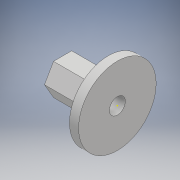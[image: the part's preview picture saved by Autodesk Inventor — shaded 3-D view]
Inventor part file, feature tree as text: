
AUTODESK INVENTOR PART (.ipt)
format: ipt  version: 2018 (Build 220112000, 112)  size: 129,536 bytes
history: native  units: mm
features: sketch x8, extrude x6
ambient origin geometry x8: Origin, YZ Plane, XZ Plane, XY Plane, X Axis, Y Axis, Z Axis, Center Point
bodies: Solid1 (feature_tree)
feature tree (14):
  extrude  "Extrusion1"  Depth=4.0mm TaperAngle=0.0deg
  extrude  "Extrusion2"  Depth=12.0mm
  sketch  "Sketch3"  dims[d6=2.0mm d7=0.0mm d8=3.0mm]
  extrude  "Extrusion3"  Depth=2.0mm
  extrude  "Extrusion4"  Depth=6.0mm
  sketch  "Sketch6"  dims[d16=3.5mm d17=12.25mm d18=0.0mm]
  extrude  "Extrusion5"  Depth=6.0mm TaperAngle=0.0deg
  extrude  "Extrusion6"  Depth=12.25mm TaperAngle=0.0deg
  sketch  "Sketch1"  dims[d0=4.0mm d1=4.0mm d2=0.0mm]
  sketch  "Sketch2"  dims[d3=2.0mm d4=0.0mm d5=12.0mm]
  sketch  "Sketch4"  dims[d9=6.0mm d10=0.0mm d11=17.0mm]
  sketch  "Sketch5"  dims[d12=2.0mm d13=0.0mm d14=6.0mm d15=0.0mm]
  sketch  "Sketch7"
  sketch  "Sketch8"
